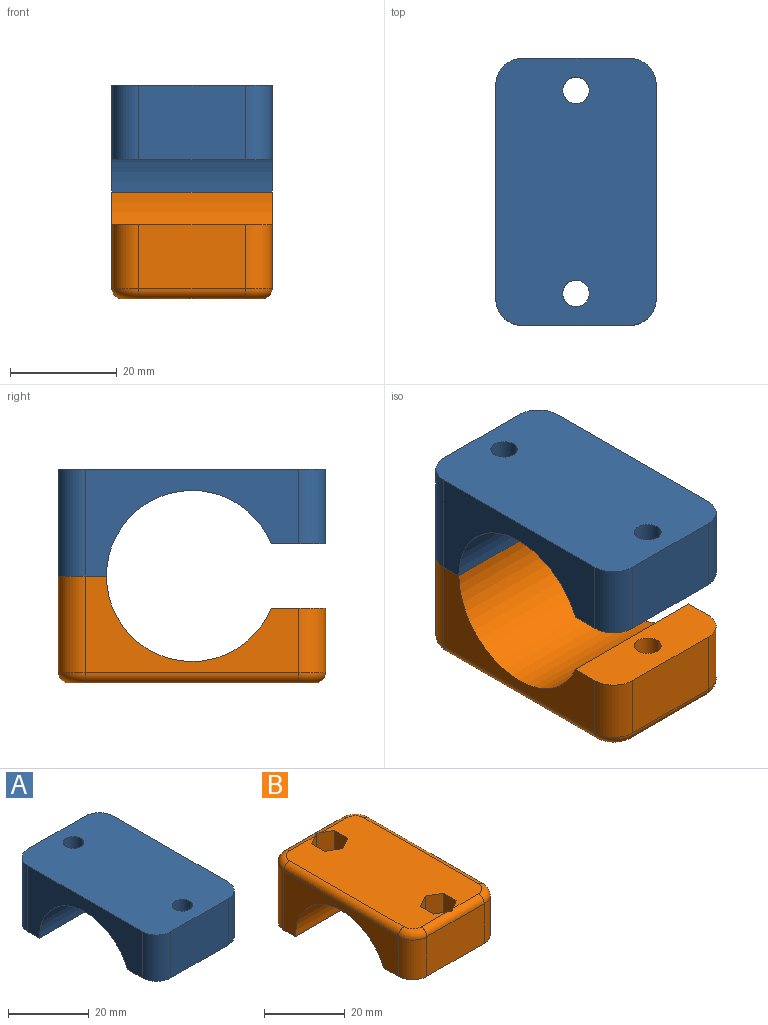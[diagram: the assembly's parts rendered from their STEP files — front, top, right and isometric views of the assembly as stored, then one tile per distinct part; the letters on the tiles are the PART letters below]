
ASSEMBLY  parts=2 mates=1
PART A: 14 faces, bbox 30x50x20 mm
  f0: plane 40x20mm, normal (1,0,0), area 371.6mm2, adj f4,f5,f8,f10,f12,f13
  f1: plane 20x20mm, normal (0,1,0), area 400mm2, adj f4,f5,f9,f10
  f2: plane 40x20mm, normal (-1,0,0), area 371.6mm2, adj f4,f5,f8,f9,f11,f13
  f3: plane 20x14mm, normal (0,-1,0), area 280mm2, adj f4,f11,f12,f13
  f4: plane 50x30mm, normal (0,0,1), area 1439.3mm2, adj f0,f1,f2,f3,f6,f7,f9,f10
  f5: plane 30x9mm, normal (0,0,-1), area 239.6mm2, adj f0,f1,f2,f6,f8,f9,f10
  f6: cylinder r=2.5mm len=20mm, axis (0,0,-1), area 314.2mm2, adj f4,f5
  f7: cylinder r=2.5mm len=14mm, axis (0,0,-1), area 219.9mm2, adj f4,f13
  f8: cylinder r=16mm len=30.83mm, axis (1,0,0), area 1323.5mm2, adj f0,f2,f5,f13
  f9: cylinder r=5mm len=20mm, axis (0,0,-1), area 157.1mm2, adj f1,f2,f4,f5
  f10: cylinder r=5mm len=20mm, axis (0,0,1), area 157.1mm2, adj f0,f1,f4,f5
  f11: cylinder r=5mm len=14mm, axis (0,0,1), area 110mm2, adj f2,f3,f4,f13
  f12: cylinder r=5mm len=14mm, axis (0,0,-1), area 110mm2, adj f0,f3,f4,f13
  f13: plane 30x10.17mm, normal (0,0,-1), area 274.7mm2, adj f0,f2,f3,f7,f8,f11,f12
PART B: 36 faces, bbox 30.8x50.8x20 mm
  f0: plane 40x18mm, normal (1,0,0), area 291.6mm2, adj f5,f6,f24,f26,f27,f35
  f1: plane 46x26mm, normal (0,0,1), area 1078.7mm2, adj f9,f10,f11,f12,f13,f14,f16,f17
  f2: plane 20x18mm, normal (0,1,0), area 360mm2, adj f5,f23,f24,f31
  f3: plane 40x18mm, normal (-1,0,0), area 291.6mm2, adj f5,f6,f23,f25,f34,f35
  f4: plane 20x12mm, normal (0,-1,0), area 240mm2, adj f25,f26,f30,f35
  f5: plane 30x9mm, normal (0,0,-1), area 239.6mm2, adj f0,f2,f3,f6,f7,f23,f24
  f6: cylinder r=16mm len=30.83mm, axis (1,0,0), area 1323.5mm2, adj f0,f3,f5,f35
  f7: cylinder r=2.5mm len=14mm, axis (0,0,-1), area 219.9mm2, adj f5,f22
  f8: cylinder r=2.5mm len=8mm, axis (0,0,-1), area 125.7mm2, adj f15,f35
  f9: plane 6x4mm, normal (-0.5,-0.87,0), area 27.7mm2, adj f1,f10,f14,f15
  f10: plane 6x4mm, normal (0.5,-0.87,0), area 27.7mm2, adj f1,f9,f11,f15
  f11: plane 6x4.62mm, normal (1,0,0), area 27.7mm2, adj f1,f10,f12,f15
  f12: plane 6.01x4.01mm, normal (0.5,0.87,0), area 27.7mm2, adj f1,f11,f13,f15,f30
  f13: plane 6.01x4.01mm, normal (-0.5,0.87,0), area 27.7mm2, adj f1,f12,f14,f15,f30
  f14: plane 6x4.62mm, normal (-1,0,0), area 27.7mm2, adj f1,f9,f13,f15
  f15: plane 9.24x8mm, normal (0,0,1), area 35.8mm2, adj f8,f9,f10,f11,f12,f13,f14
  f16: plane 6.01x4.01mm, normal (-0.5,-0.87,0), area 27.7mm2, adj f1,f17,f21,f22,f31
  f17: plane 6.01x4.01mm, normal (0.5,-0.87,0), area 27.7mm2, adj f1,f16,f18,f22,f31
  f18: plane 6x4.62mm, normal (1,0,0), area 27.7mm2, adj f1,f17,f19,f22
  f19: plane 6x4mm, normal (0.5,0.87,0), area 27.7mm2, adj f1,f18,f20,f22
  f20: plane 6x4mm, normal (-0.5,0.87,0), area 27.7mm2, adj f1,f19,f21,f22
  f21: plane 6x4.62mm, normal (-1,0,0), area 27.7mm2, adj f1,f16,f20,f22
  f22: plane 9.24x8mm, normal (0,0,1), area 35.8mm2, adj f7,f16,f17,f18,f19,f20,f21
  f23: cylinder r=5mm len=18mm, axis (0,0,-1), area 141.4mm2, adj f2,f3,f5,f33
  f24: cylinder r=5mm len=18mm, axis (0,0,1), area 141.4mm2, adj f0,f2,f5,f29
  f25: cylinder r=5mm len=12mm, axis (0,0,1), area 94.2mm2, adj f3,f4,f32,f35
  f26: cylinder r=5mm len=12mm, axis (0,0,-1), area 94.2mm2, adj f0,f4,f28,f35
  f27: cylinder r=2mm len=40mm, axis (0,-1,0), area 125.7mm2, adj f0,f1,f28,f29
  f28: torus R=3mm, axis (0,0,1), area 21.1mm2, adj f1,f26,f27,f30
  f29: torus R=3mm, axis (0,0,1), area 21.1mm2, adj f1,f24,f27,f31
  f30: cylinder r=2mm len=20mm, axis (-1,0,0), area 62.2mm2, adj f1,f4,f12,f13,f28,f32
  f31: cylinder r=2mm len=20mm, axis (1,0,0), area 62.2mm2, adj f1,f2,f16,f17,f29,f33
  f32: torus R=3mm, axis (0,0,1), area 21.1mm2, adj f1,f25,f30,f34
  f33: torus R=3mm, axis (0,0,1), area 21.1mm2, adj f1,f23,f31,f34
  f34: cylinder r=2mm len=40mm, axis (0,1,0), area 125.7mm2, adj f1,f3,f32,f33
  f35: plane 30x10.17mm, normal (0,0,-1), area 274.7mm2, adj f0,f3,f4,f6,f8,f25,f26
PLACE A t=(37.43,60.86,-3.11)mm
PLACE B rot(axis=(0,1,0),180deg) t=(37.43,60.86,-3.11)mm
MATE slider A.f6 <-> B.f7  axis (0,0,-1) through (37.43,79.86,-3.11)mm
